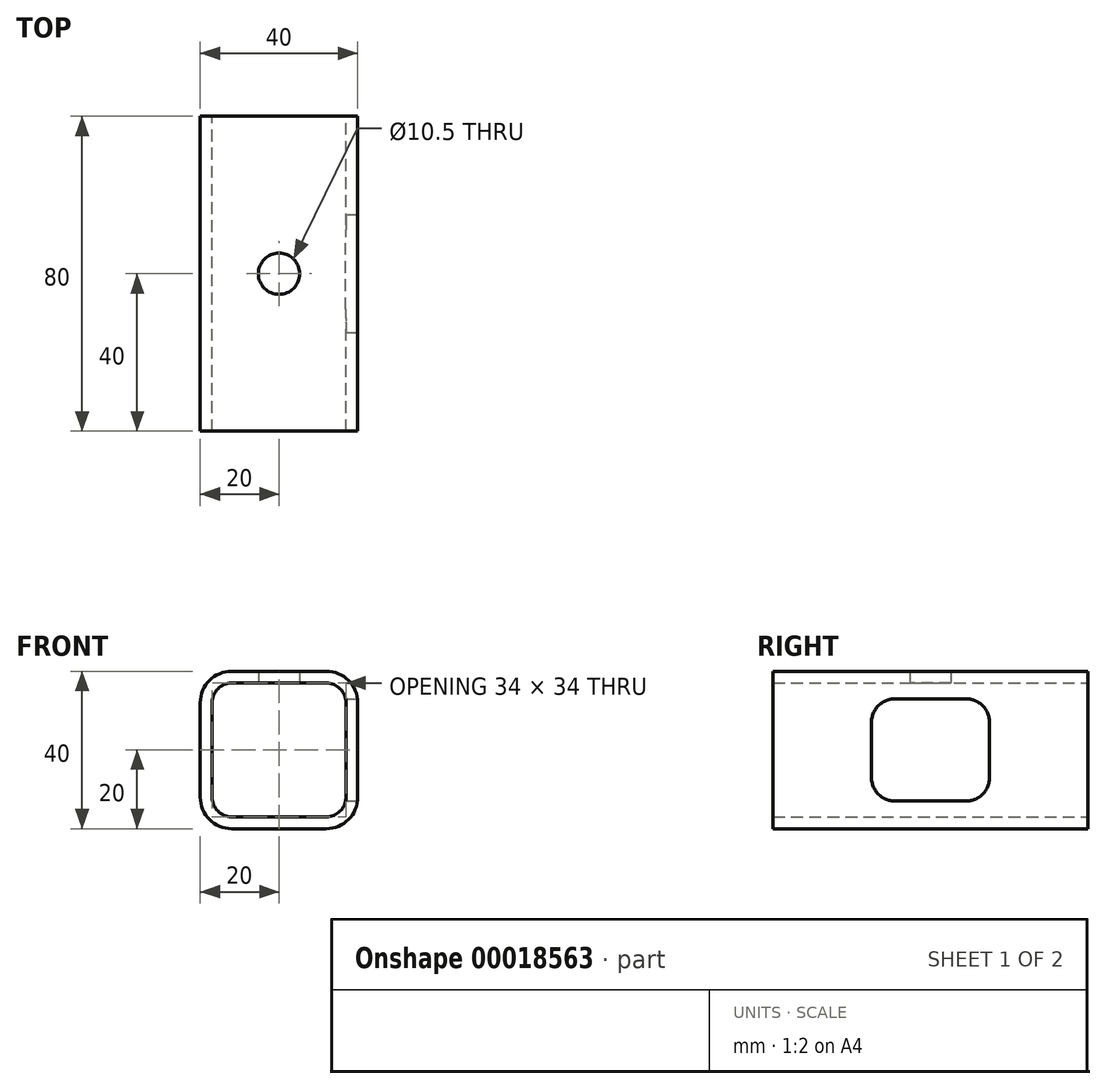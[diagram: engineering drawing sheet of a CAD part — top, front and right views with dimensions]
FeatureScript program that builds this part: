
annotation { "Feature Type Name" : "Feature", "Feature Type Description" : "" }
export const myFeature = defineFeature(function(context is Context, id is Id, definition is map)
    precondition{}
    {
        {
            var Q0;
            Q0=qCreatedBy(makeId("Front.planeOp"),FACE);
            var sketch = newSketch(context, id + "F0", { "sketchPlane" : qUnion([Q0])});
            skLineSegment(sketch, "E0.bottom", {"start": v(-12, 20) * mm, "end": v(12, 20) * mm});
            skLineSegment(sketch, "E0.top", {"start": v(-12, -20) * mm, "end": v(12, -20) * mm});
            skLineSegment(sketch, "E0.left", {"start": v(-20, 12) * mm, "end": v(-20, -12) * mm});
            skLineSegment(sketch, "E0.right", {"start": v(20, 12) * mm, "end": v(20, -12) * mm});
            skPoint(sketch, "E1.visualSharp", {"position": v(20, 20) * mm});
            skArc(sketch, "E1.filletArc", {"start": v(20, 12) * mm, "mid": v(17.66, 17.66) * mm, "end": v(12, 20) * mm});
            skPoint(sketch, "E2.visualSharp", {"position": v(-20, 20) * mm});
            skArc(sketch, "E2.filletArc", {"start": v(-12, 20) * mm, "mid": v(-17.66, 17.66) * mm, "end": v(-20, 12) * mm});
            skPoint(sketch, "E3.visualSharp", {"position": v(-20, -20) * mm});
            skArc(sketch, "E3.filletArc", {"start": v(-20, -12) * mm, "mid": v(-17.66, -17.66) * mm, "end": v(-12, -20) * mm});
            skPoint(sketch, "E4.visualSharp", {"position": v(20, -20) * mm});
            skArc(sketch, "E4.filletArc", {"start": v(12, -20) * mm, "mid": v(17.66, -17.66) * mm, "end": v(20, -12) * mm});
            skArc(sketch, "E5.0", {"start": v(-12, 17) * mm, "mid": v(-15.54, 15.54) * mm, "end": v(-17, 12) * mm});
            skLineSegment(sketch, "E5.1", {"start": v(-17, 12) * mm, "end": v(-17, -12) * mm});
            skArc(sketch, "E5.2", {"start": v(-17, -12) * mm, "mid": v(-15.54, -15.54) * mm, "end": v(-12, -17) * mm});
            skLineSegment(sketch, "E5.3", {"start": v(-12, -17) * mm, "end": v(12, -17) * mm});
            skArc(sketch, "E5.4", {"start": v(12, -17) * mm, "mid": v(15.54, -15.54) * mm, "end": v(17, -12) * mm});
            skLineSegment(sketch, "E5.5", {"start": v(-12, 17) * mm, "end": v(12, 17) * mm});
            skLineSegment(sketch, "E5.6", {"start": v(17, 12) * mm, "end": v(17, -12) * mm});
            skArc(sketch, "E5.7", {"start": v(17, 12) * mm, "mid": v(15.54, 15.54) * mm, "end": v(12, 17) * mm});
            skSolve(sketch);
        }
        {
            var Q0;
            Q0=makeQuery(id+"F0.imprint","IMPRINT",FACE,{"disambiguationData":[TD([[makeQuery(id+"F0.imprint","IMPRINT",EDGE,{"derivedFrom":sQuery(id+"F0.wireOp",EDGE,"E0.bottom")}),-1.0]])]});
            extrude(context, id + "F1", {"entities" : qUnion([Q0]), "endBound" : BoundingType.SYMMETRIC, "depth" : 80 * mm, "hasSecondDirection" : true, "secondDirectionOppositeDirection" : true, "secondDirectionDepth" : 25 * mm});
        }
        {
            var Q0;
            Q0=qCreatedBy(makeId("Top.planeOp"),FACE);
            var sketch = newSketch(context, id + "F2", { "sketchPlane" : qUnion([Q0])});
            skCircle(sketch, "E6", {"center": v(0, 0) * mm, "radius": 5.25 * mm});
            skSolve(sketch);
        }
        {
            var Q0;
            Q0=makeQuery(id+"F2.imprint","IMPRINT",FACE,{"disambiguationData":[TD([[makeQuery(id+"F2.imprint","IMPRINT",EDGE,{"derivedFrom":sQuery(id+"F2.wireOp",EDGE,"E6")}),1.0]])]});
            extrude(context, id + "F3", {"entities" : qUnion([Q0]), "operationType" : NewBodyOperationType.REMOVE, "depth" : 48.6 * mm});
        }
        {
            var Q0;
            Q0=makeQuery(id+"F1.opExtrude","SWEPT_FACE",FACE,{"disambiguationData":[OSD([sQuery(id+"F0.wireOp",EDGE,"E0.right")])]});
            var sketch = newSketch(context, id + "F4", { "sketchPlane" : qUnion([Q0])});
            skLineSegment(sketch, "E7.bottom", {"start": v(-15, 13) * mm, "end": v(15, 13) * mm});
            skLineSegment(sketch, "E7.top", {"start": v(-15, -13) * mm, "end": v(15, -13) * mm});
            skLineSegment(sketch, "E7.left", {"start": v(-15, 13) * mm, "end": v(-15, -13) * mm});
            skLineSegment(sketch, "E7.right", {"start": v(15, 13) * mm, "end": v(15, -13) * mm});
            skSolve(sketch);
        }
        {
            var Q0;
            {var subQ0=sQuery(id+"F0.wireOp",EDGE,"E0.right");var subQ4=sQuery(id+"F4.wireOp",EDGE,"E7.left");var subQ6=makeQuery(id+"F1.opExtrude","SWEPT_EDGE",EDGE,{"disambiguationData":[OSD([subQ0,sQuery(id+"F0.wireOp",EDGE,"E1.filletArc")])]});var subQ8=makeQuery(id+"F4.imprint","INTERSECT",VERTEX,{"derivedFrom":[subQ6,subQ4]});Q0=makeQuery(id+"F4.imprint","IMPRINT",FACE,{"disambiguationData":[TD([[makeQuery(id+"F4.imprint","IMPRINT",EDGE,{"disambiguationData":[TD([[subQ8,-1.0]])],"derivedFrom":subQ4}),1.0]])]});}
            var Q1;
            {var subQ5=sQuery(id+"F4.wireOp",EDGE,"E7.top");Q1=makeQuery(id+"F4.imprint","IMPRINT",FACE,{"disambiguationData":[TD([[makeQuery(id+"F4.imprint","IMPRINT",EDGE,{"derivedFrom":subQ5}),1.0]])]});}
            var Q2;
            {var subQ3=sQuery(id+"F4.wireOp",EDGE,"E7.bottom");Q2=makeQuery(id+"F4.imprint","IMPRINT",FACE,{"disambiguationData":[TD([[makeQuery(id+"F4.imprint","IMPRINT",EDGE,{"derivedFrom":subQ3}),-1.0]])]});}
            extrude(context, id + "F5", {"entities" : qUnion([Q0, Q1, Q2]), "operationType" : NewBodyOperationType.REMOVE, "oppositeDirection" : true, "depth" : 8 * mm});
        }
        {
            var Q0;
            Q0=makeQuery(id+"F5.boolean.opBoolean","COPY",EDGE,{"derivedFrom":makeQuery(id+"F5.opExtrude","SWEPT_EDGE",EDGE,{"disambiguationData":[OSD([sQuery(id+"F4.wireOp",EDGE,"E7.bottom"),sQuery(id+"F4.wireOp",EDGE,"E7.right")])]})});
            var Q1;
            Q1=makeQuery(id+"F5.boolean.opBoolean","COPY",EDGE,{"derivedFrom":makeQuery(id+"F5.opExtrude","SWEPT_EDGE",EDGE,{"disambiguationData":[OSD([sQuery(id+"F4.wireOp",EDGE,"E7.top"),sQuery(id+"F4.wireOp",EDGE,"E7.right")])]})});
            var Q2;
            Q2=makeQuery(id+"F5.boolean.opBoolean","COPY",EDGE,{"derivedFrom":makeQuery(id+"F5.opExtrude","SWEPT_EDGE",EDGE,{"disambiguationData":[OSD([sQuery(id+"F4.wireOp",EDGE,"E7.top"),sQuery(id+"F4.wireOp",EDGE,"E7.left")])]})});
            var Q3;
            Q3=makeQuery(id+"F5.boolean.opBoolean","COPY",EDGE,{"derivedFrom":makeQuery(id+"F5.opExtrude","SWEPT_EDGE",EDGE,{"disambiguationData":[OSD([sQuery(id+"F4.wireOp",EDGE,"E7.bottom"),sQuery(id+"F4.wireOp",EDGE,"E7.left")])]})});
            fillet(context, id + "F6", {"entities" : qUnion([Q0, Q1, Q2, Q3]), "radius" : 6 * mm, "tangentPropagation" : true, "allowEdgeOverflow" : false});
        }
    });
